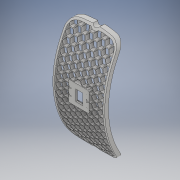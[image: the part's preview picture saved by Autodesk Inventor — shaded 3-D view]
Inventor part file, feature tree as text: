
AUTODESK INVENTOR PART (.ipt)
format: ipt  version: 2019 (Build 230136000, 136)  size: 5,053,952 bytes
history: native  units: mm
features: extrude x7, sketch x5, other x3, pattern_linear x1, plane x1, projected_geometry x1
ambient origin geometry x8: Origin, YZ Plane, XZ Plane, XY Plane, X Axis, Y Axis, Z Axis, Center Point
bodies: Volumenkörper2 (feature_tree), Volumenkörper4 (feature_tree), Volumenkörper1 (feature_tree)
feature tree (18):
  other  "Brille_Glas_Zusammenbau.ipt"
  sketch  "Skizze1"  dims[d0=10.0mm d2=1.0mm d3=60.0mm d4=0.0mm]
  sketch  "Skizze3"  dims[d11=250.0mm d13=11.0mm d14=140.0mm d16=11.0mm]
  extrude  "Extrusion1"  Depth=1.0mm
  pattern_linear  "Rechteckige Anordnung2"  Count1=6 Spacing1=0.0mm
  sketch  "Skizze10"  dims[d25=0.5mm d26=3.5mm]
  extrude  "Extrusion5"  Depth=140.0mm
  extrude  "Extrusion6"  Depth=3.5mm
  extrude  "Extrusion7"  Depth=60.0mm TaperAngle=0.0deg
  sketch  "Skizze11"  dims[d27=60.0mm d28=0.0mm d29=60.0mm d30=0.0mm]
  extrude  "Extrusion8"  Depth=25.0mm
  plane  "Arbeitsebene1"
  sketch  "Skizze12"  dims[d31=60.0mm d32=0.0mm d33=25.0mm d34=24.0mm d35=0.0mm d36=0.0mm d37=45.066mm d40=2.5mm d41=4.0mm d42=6.0mm d43=7.7mm d44=2.5mm d45=0.0mm d46=4.0mm d47=2.0mm d48=4.0mm d49=0.0mm]
  extrude  "Extrusion9"  Depth=24.0mm
  extrude  "Extrusion10"  TaperAngle=0.0deg  [1 undecoded]
  other  "Volumenkörper7::Brille_Glas_Zusammenbau.ipt"
  other  "Bezeichnung1"
  projected_geometry  "Projizierte Kontur1"
note: 1 required parameter value undecoded (feature->parameter linkage not recoverable at this tier; creation-order binding heuristic only, values carry confidence <= 0.55)
